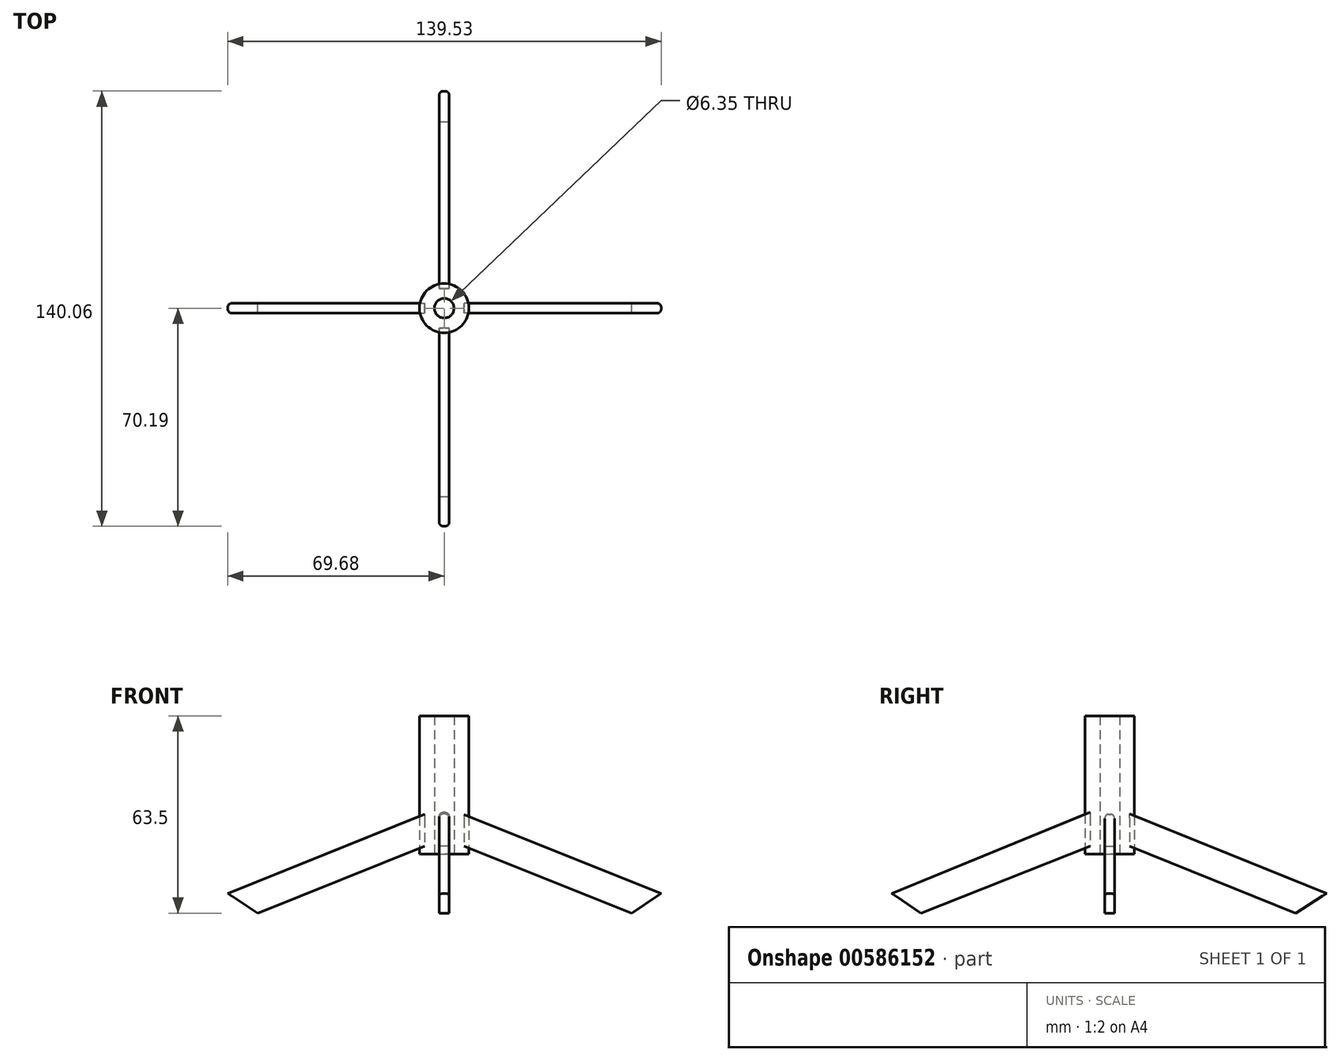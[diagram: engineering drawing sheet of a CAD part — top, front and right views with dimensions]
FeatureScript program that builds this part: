
annotation { "Feature Type Name" : "Feature", "Feature Type Description" : "" }
export const myFeature = defineFeature(function(context is Context, id is Id, definition is map)
    precondition{}
    {
        {
            var Q0;
            Q0=qCreatedBy(makeId("Top.planeOp"),FACE);
            var sketch = newSketch(context, id + "F0", { "sketchPlane" : qUnion([Q0])});
            skCircle(sketch, "E0", {"center": v(0, 0) * mm, "radius": 69.85 * mm});
            skCircle(sketch, "E1", {"center": v(0, 0) * mm, "radius": 60.33 * mm});
            skCircle(sketch, "E2", {"center": v(0, 0) * mm, "radius": 7.94 * mm});
            skCircle(sketch, "E3", {"center": v(0, 0) * mm, "radius": 3.18 * mm});
            skSolve(sketch);
        }
        {
            var Q0;
            Q0=makeQuery(id+"F0.imprint","IMPRINT",FACE,{"disambiguationData":[TD([[makeQuery(id+"F0.imprint","IMPRINT",EDGE,{"derivedFrom":sQuery(id+"F0.wireOp",EDGE,"E2")}),1.0]])]});
            extrude(context, id + "F1", {"entities" : qUnion([Q0]), "depth" : 63.5 * mm, "offsetDistance" : 25.4 * mm});
        }
        {
            var Q0;
            Q0=qCreatedBy(makeId("Front.planeOp"),FACE);
            var sketch = newSketch(context, id + "F2", { "sketchPlane" : qUnion([Q0])});
            skLineSegment(sketch, "E4", {"start": v(-69.68, 6.35) * mm, "end": v(-6.35, 31.82) * mm});
            skLineSegment(sketch, "E5", {"start": v(-60.03, 0) * mm, "end": v(-6.35, 21.6) * mm});
            skLineSegment(sketch, "E6", {"start": v(69.85, 6.35) * mm, "end": v(6.35, 31.75) * mm});
            skLineSegment(sketch, "E7", {"start": v(60.32, 0) * mm, "end": v(6.35, 21.6) * mm});
            skLineSegment(sketch, "E8", {"start": v(-69.68, 6.35) * mm, "end": v(-60.03, 0) * mm});
            skLineSegment(sketch, "E9", {"start": v(60.32, 0) * mm, "end": v(69.85, 6.35) * mm});
            skLineSegment(sketch, "E10", {"start": v(6.35, 31.75) * mm, "end": v(6.35, 21.59) * mm});
            skLineSegment(sketch, "E11", {"start": v(-6.35, 31.82) * mm, "end": v(-6.35, 21.6) * mm});
            skSolve(sketch);
        }
        {
            var Q0;
            Q0 = qSketchRegion(id + "F2", true);
            extrude(context, id + "F3", {"entities" : qUnion([Q0]), "depth" : 3.17 * mm, "offsetDistance" : 25.4 * mm, "symmetric" : true});
        }
        {
            var Q0;
            Q0=qCreatedBy(makeId("Right.planeOp"),FACE);
            var sketch = newSketch(context, id + "F4", { "sketchPlane" : qUnion([Q0])});
            skLineSegment(sketch, "E12", {"start": v(69.87, 6.35) * mm, "end": v(6.35, 31.96) * mm});
            skLineSegment(sketch, "E13", {"start": v(6.35, 31.96) * mm, "end": v(6.35, 21.59) * mm});
            skLineSegment(sketch, "E14", {"start": v(6.35, 21.6) * mm, "end": v(59.89, 0) * mm});
            skLineSegment(sketch, "E15", {"start": v(59.89, 0) * mm, "end": v(69.87, 6.35) * mm});
            skLineSegment(sketch, "E16", {"start": v(-70.19, 6.35) * mm, "end": v(-6.35, 32.47) * mm});
            skLineSegment(sketch, "E17", {"start": v(-6.35, 32.47) * mm, "end": v(-6.35, 21.59) * mm});
            skLineSegment(sketch, "E18", {"start": v(-6.35, 21.6) * mm, "end": v(-60.71, 0) * mm});
            skLineSegment(sketch, "E19", {"start": v(-60.71, 0) * mm, "end": v(-70.19, 6.35) * mm});
            skSolve(sketch);
        }
        {
            var Q0;
            Q0 = qSketchRegion(id + "F4", true);
            extrude(context, id + "F5", {"entities" : qUnion([Q0]), "depth" : 3.17 * mm, "offsetDistance" : 25.4 * mm, "symmetric" : true});
        }
        {
            var Q0;
            Q0=makeQuery(id+"F0.imprint","IMPRINT",FACE,{"disambiguationData":[TD([[makeQuery(id+"F0.imprint","IMPRINT",EDGE,{"derivedFrom":sQuery(id+"F0.wireOp",EDGE,"E2")}),1.0]])]});
            extrude(context, id + "F6", {"entities" : qUnion([Q0]), "operationType" : NewBodyOperationType.REMOVE, "depth" : 19.05 * mm, "offsetDistance" : 25.4 * mm});
        }
        {
            var Q0;
            Q0=makeQuery(id+"F3.opExtrude","CAP_EDGE",EDGE,{"disambiguationData":[OSD([sQuery(id+"F2.wireOp",EDGE,"E4")])],"isStart":true});
            var Q1;
            Q1=makeQuery(id+"F3.opExtrude","CAP_EDGE",EDGE,{"disambiguationData":[OSD([sQuery(id+"F2.wireOp",EDGE,"E4")])],"isStart":false});
            var Q2;
            Q2=makeQuery(id+"F5.opExtrude","CAP_EDGE",EDGE,{"disambiguationData":[OSD([sQuery(id+"F4.wireOp",EDGE,"E12")])],"isStart":false});
            var Q3;
            Q3=makeQuery(id+"F5.opExtrude","CAP_EDGE",EDGE,{"disambiguationData":[OSD([sQuery(id+"F4.wireOp",EDGE,"E12")])],"isStart":true});
            var Q4;
            Q4=makeQuery(id+"F3.opExtrude","CAP_EDGE",EDGE,{"disambiguationData":[OSD([sQuery(id+"F2.wireOp",EDGE,"E6")])],"isStart":true});
            var Q5;
            Q5=makeQuery(id+"F3.opExtrude","CAP_EDGE",EDGE,{"disambiguationData":[OSD([sQuery(id+"F2.wireOp",EDGE,"E6")])],"isStart":false});
            var Q6;
            Q6=makeQuery(id+"F5.opExtrude","CAP_EDGE",EDGE,{"disambiguationData":[OSD([sQuery(id+"F4.wireOp",EDGE,"E16")])],"isStart":true});
            var Q7;
            Q7=makeQuery(id+"F5.opExtrude","CAP_EDGE",EDGE,{"disambiguationData":[OSD([sQuery(id+"F4.wireOp",EDGE,"E16")])],"isStart":false});
            fillet(context, id + "F7", {"entities" : qUnion([Q0, Q1, Q2, Q3, Q4, Q5, Q6, Q7]), "radius" : 1.27 * mm, "tangentPropagation" : true, "allowEdgeOverflow" : false});
        }
    });
